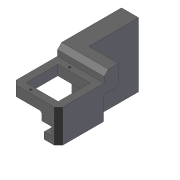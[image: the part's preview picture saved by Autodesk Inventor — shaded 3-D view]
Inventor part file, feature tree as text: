
AUTODESK INVENTOR PART (.ipt)
format: ipt  version: 2020 (Build 240168000, 168)  size: 152,576 bytes
history: mixed  units: mm
features: extrude x2, sketch x2, other x1, imported_body x1
ambient origin geometry x8: Origin, YZ Plane, XZ Plane, XY Plane, X Axis, Y Axis, Z Axis, Center Point
bodies: Solid1 (imported_parasolid)
feature tree (6):
  extrude  "Extrusion1"  Depth=24.0mm TaperAngle=0.0deg
  extrude  "Extrusion2"  [1 undecoded]
  sketch  "Sketch1"  dims[d0=25.0mm d1=0.0mm d2=24.0mm d3=0.0mm]
  sketch  "Sketch2"
  other  "Cut-Extrude3"
  imported_body  NMx_Import_Brep_tag  [imported B-rep: ~40 faces, bbox_mm=[32.8, 45.14, 77.1]]
note: 1 required parameter value undecoded (feature->parameter linkage not recoverable at this tier; creation-order binding heuristic only, values carry confidence <= 0.55)
